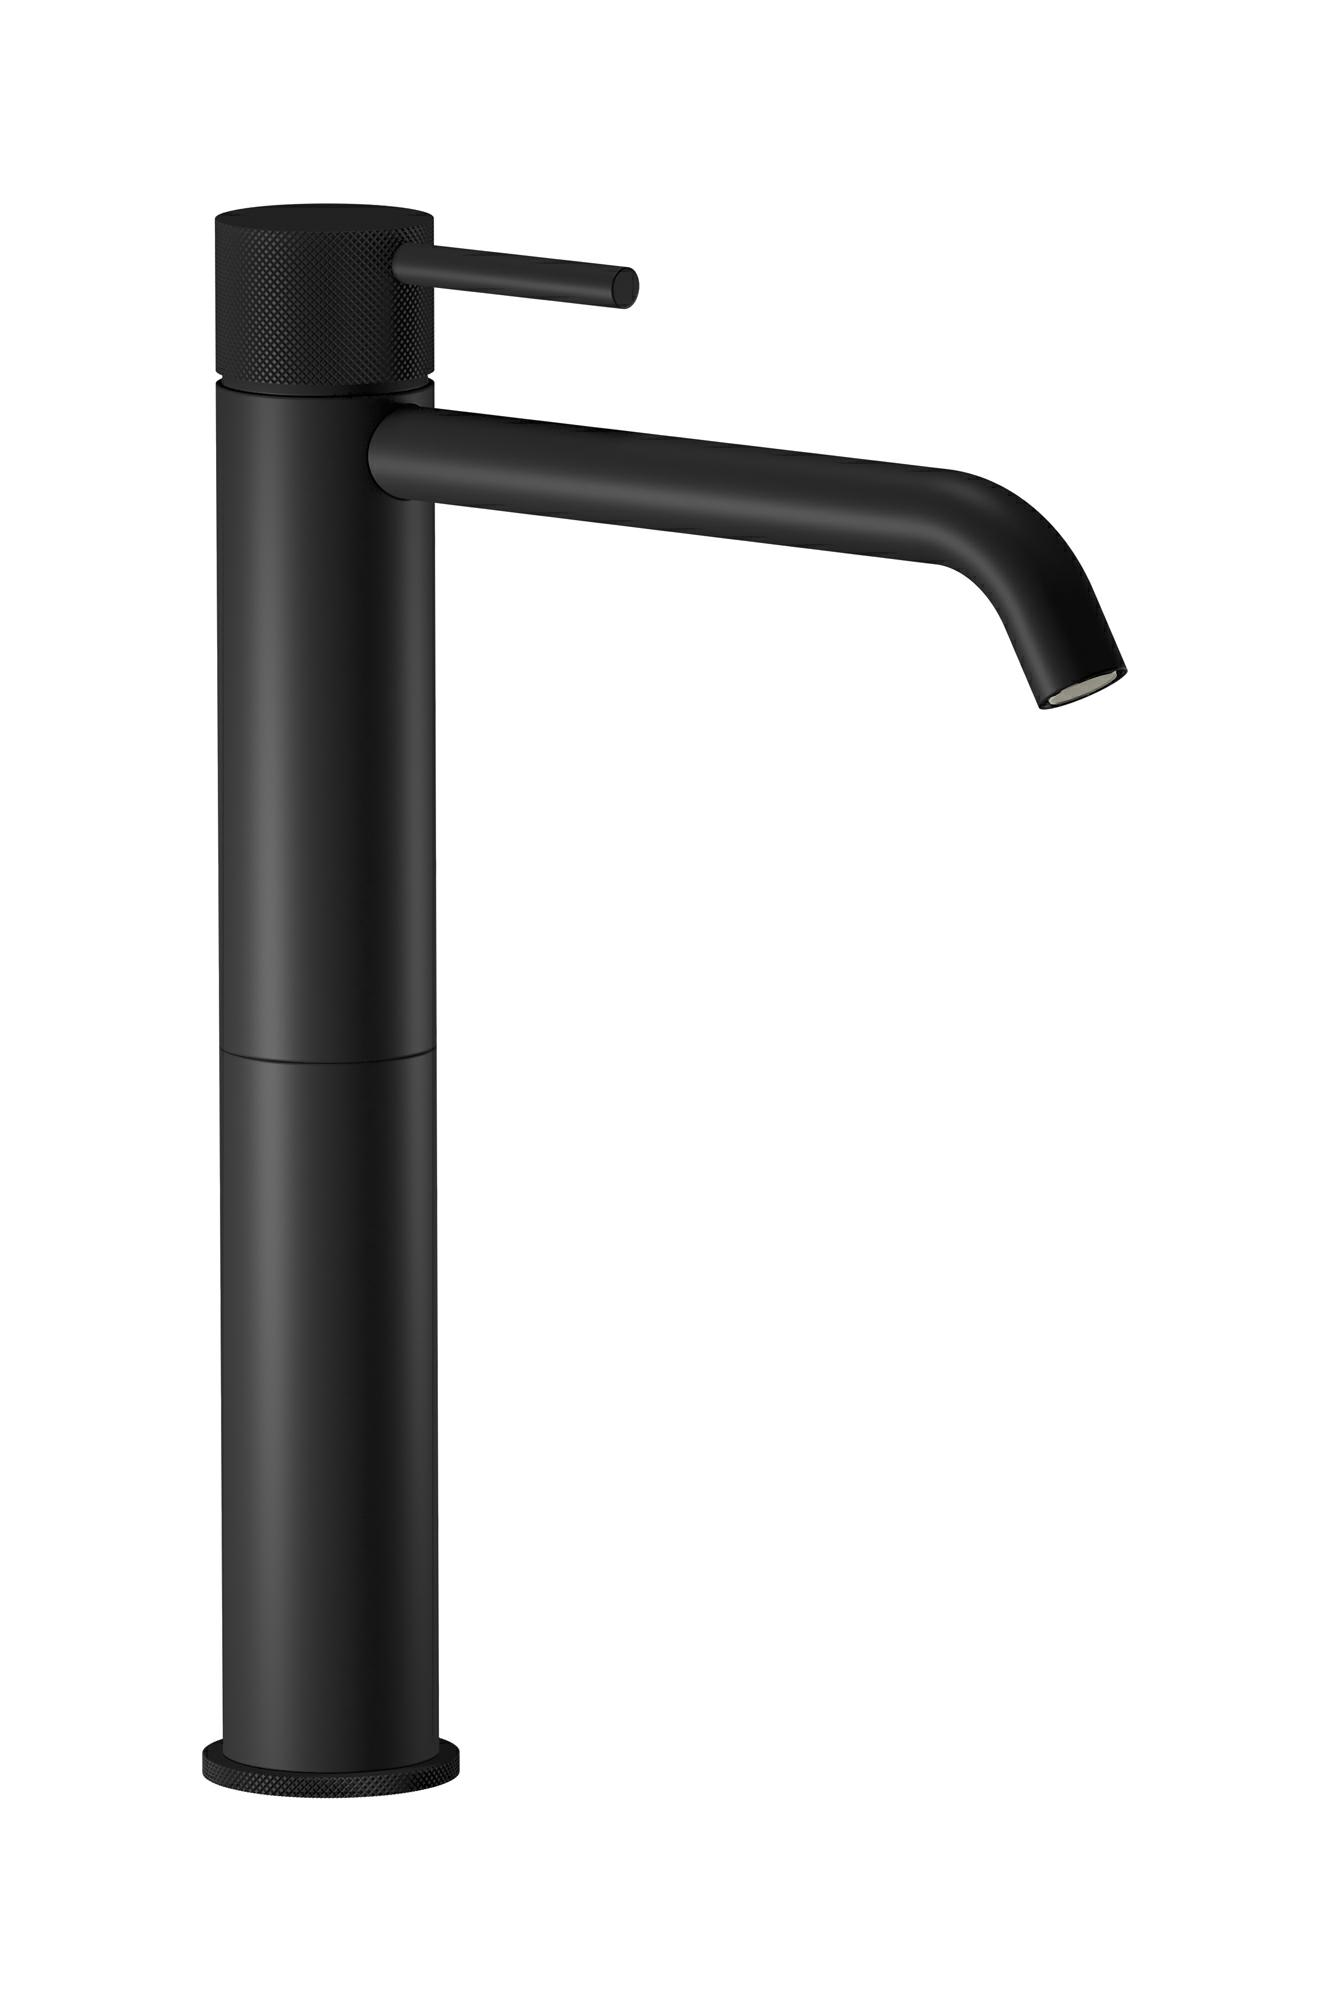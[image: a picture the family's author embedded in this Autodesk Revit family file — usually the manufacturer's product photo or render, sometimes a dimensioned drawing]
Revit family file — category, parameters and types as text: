
# Revit family: ID370
name_source: partatom
category: Apparecchi idraulici
units: mm (PartAtom-declared; Revit-internal decimal feet)

## family parameters
Basato su piano di lavoro = No
Condiviso = No
Mantieni orientamento annotazione = No
Numero OmniClass = 23.45.55.17
Punto di calcolo locali = No
Quota connettore circolare = Usa diametro
Sempre verticale = Sì
Taglio con vuoti quando caricato = No
Tipo di parte = Normale
Titolo OmniClass = Mixing Faucets

## types (12) — shared parameters
Cold water inlet = 10 mm  [stored 0.0328084 ft]
Commenti sul tipo = kitchen mixer
Connessione CW = No
Connessione HW = No
Connessione di scarico = No
Connessione di ventilazione = No
Descrizione = Single lever kitchen mixer
Hot water inlet = 10 mm  [stored 0.0328084 ft]
Produttore = IB Rubinetterie S.p.A.
URL = https://www.weareib.it
zero-valued in all types: Prospetto di default

## per-type parameters (varying)
| type | Finishes surface | Immagine tipo | Modello |
| Chrome | IB_Chrome | ID370CC.jpg | ID370CC |
| Brushed nickel | IB_Brushed nickel | ID370SS.jpg | ID370SS |
| Natural brass | IB_Brass | ID370ON.jpg | ID370ON |
| Matt black | IB_matt black | ID370NP.jpg | ID370NP |
| Black chrome | IB_Black chrome | ID370CF.jpg | ID370CF |
| Brushed black chrome | IB_Brushed black chrome | ID370CS.jpg | ID370CS |
| Pale gold | IB_Pale gold | ID370II.jpg | ID370II |
| Brushed pale gold | IB_brushed pale gold | ID370IS.jpg | ID370IS |
| Rose gold | IB_Rose gold | ID370RS.jpg | ID370RS |
| Brushed rose gold | IB_Brushed rose gold | ID370SR.jpg | ID370SR |
| Gold | IB_gold | ID370OO.jpg | ID370OO |
| Brushed gold | IB_brushed gold | ID370OS.jpg | ID370OS |

note: [stored X ft] marks values corroborated as IEEE doubles in the binary element streams (Revit-internal decimal feet)
